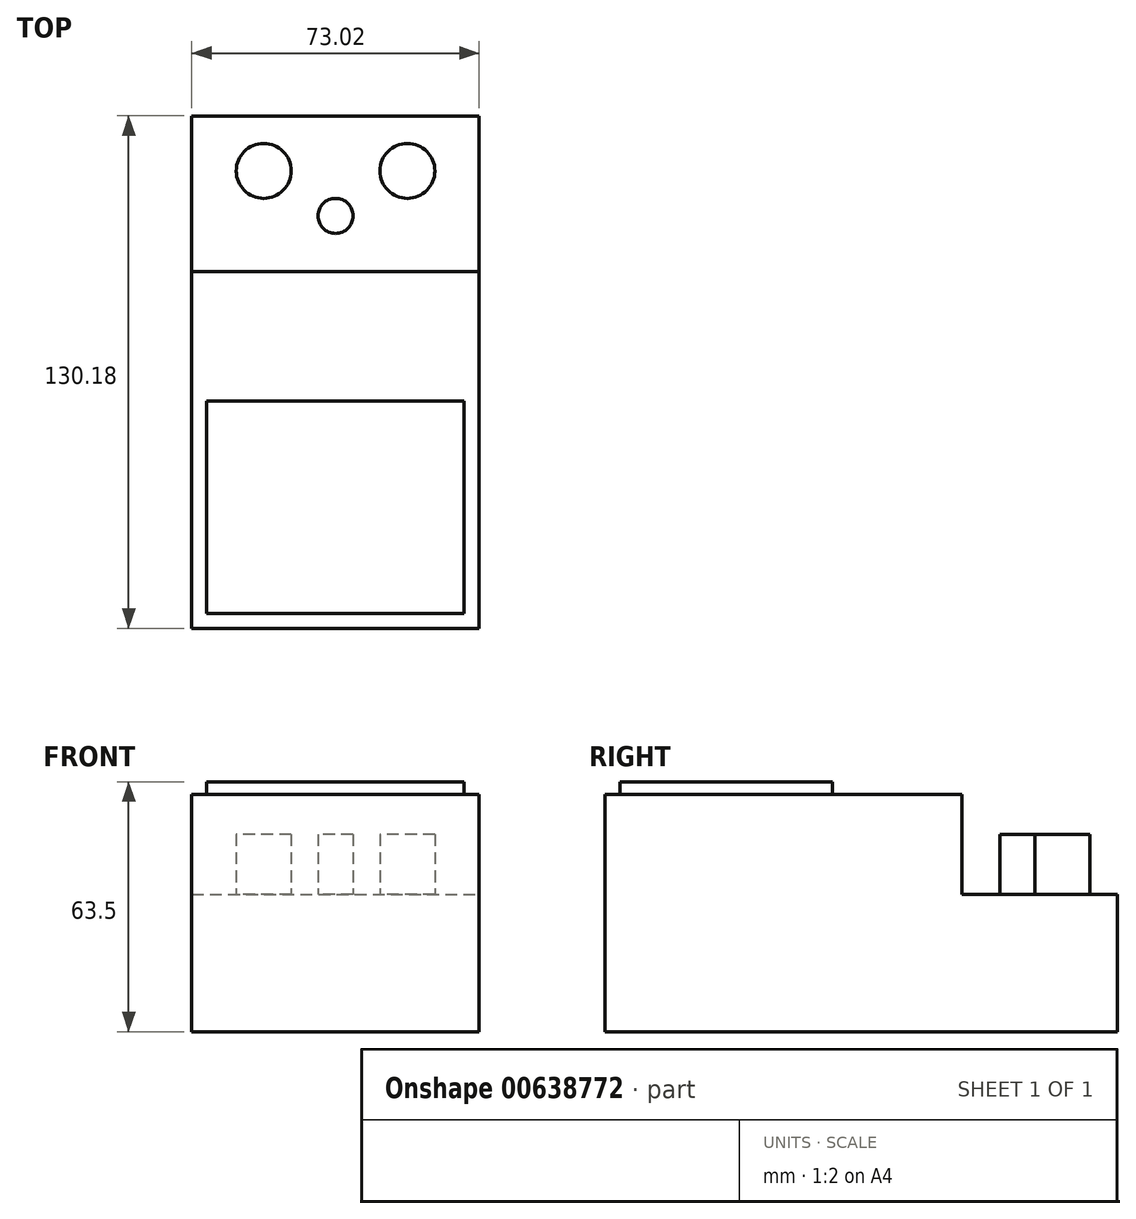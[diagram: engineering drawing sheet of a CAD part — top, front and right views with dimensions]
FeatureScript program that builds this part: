
annotation { "Feature Type Name" : "Feature", "Feature Type Description" : "" }
export const myFeature = defineFeature(function(context is Context, id is Id, definition is map)
    precondition{}
    {
        {
            var Q0;
            Q0=qCreatedBy(makeId("Top.planeOp"),FACE);
            var sketch = newSketch(context, id + "F0", { "sketchPlane" : qUnion([Q0])});
            skLineSegment(sketch, "E0.bottom", {"start": v(-36.51, 65.09) * mm, "end": v(36.51, 65.09) * mm});
            skLineSegment(sketch, "E0.top", {"start": v(-36.51, -65.09) * mm, "end": v(36.51, -65.09) * mm});
            skLineSegment(sketch, "E0.left", {"start": v(-36.51, 65.09) * mm, "end": v(-36.51, -65.09) * mm});
            skLineSegment(sketch, "E0.right", {"start": v(36.51, 65.09) * mm, "end": v(36.51, -65.09) * mm});
            skPoint(sketch, "E0.middle", {"position": v(0, 0) * mm});
            skLineSegment(sketch, "E1", {"start": v(-36.51, 25.5) * mm, "end": v(36.51, 25.5) * mm});
            skSolve(sketch);
        }
        {
            var Q0;
            {var subQ0=sQuery(id+"F0.wireOp",EDGE,"E0.top");Q0=makeQuery(id+"F0.imprint","IMPRINT",FACE,{"disambiguationData":[TD([[makeQuery(id+"F0.imprint","IMPRINT",EDGE,{"derivedFrom":subQ0}),1.0]])]});}
            extrude(context, id + "F1", {"entities" : qUnion([Q0]), "depth" : 60.32 * mm, "offsetDistance" : 25.4 * mm});
        }
        {
            var Q0;
            Q0 = qSketchRegion(id + "F0", true);
            extrude(context, id + "F2", {"entities" : qUnion([Q0]), "operationType" : NewBodyOperationType.ADD, "depth" : 34.92 * mm, "offsetDistance" : 25.4 * mm});
        }
        {
            var Q0;
            Q0=makeQuery(id+"F1.opExtrude","CAP_FACE",FACE,{"disambiguationData":[OSD([sQuery(id+"F0.wireOp",EDGE,"E0.top"),sQuery(id+"F0.wireOp",EDGE,"E0.left"),sQuery(id+"F0.wireOp",EDGE,"E0.right"),sQuery(id+"F0.wireOp",EDGE,"E1")])],"isStart":false});
            var sketch = newSketch(context, id + "F3", { "sketchPlane" : qUnion([Q0])});
            skLineSegment(sketch, "E2.bottom", {"start": v(-32.7, -61.28) * mm, "end": v(32.7, -61.28) * mm});
            skLineSegment(sketch, "E2.top", {"start": v(-32.7, -7.32) * mm, "end": v(32.7, -7.32) * mm});
            skLineSegment(sketch, "E2.left", {"start": v(-32.7, -61.28) * mm, "end": v(-32.7, -7.32) * mm});
            skLineSegment(sketch, "E2.right", {"start": v(32.7, -61.28) * mm, "end": v(32.7, -7.32) * mm});
            skSolve(sketch);
        }
        {
            var Q0;
            Q0=makeQuery(id+"F3.imprint","IMPRINT",FACE,{"disambiguationData":[TD([[makeQuery(id+"F3.imprint","IMPRINT",EDGE,{"derivedFrom":sQuery(id+"F3.wireOp",EDGE,"E2.bottom")}),1.0]])]});
            extrude(context, id + "F4", {"entities" : qUnion([Q0]), "operationType" : NewBodyOperationType.ADD, "depth" : 3.17 * mm, "offsetDistance" : 25.4 * mm});
        }
        {
            var Q0;
            Q0=makeQuery(id+"F2.opExtrude","CAP_FACE",FACE,{"disambiguationData":[OSD([sQuery(id+"F0.wireOp",EDGE,"E0.bottom"),sQuery(id+"F0.wireOp",EDGE,"E0.top"),sQuery(id+"F0.wireOp",EDGE,"E0.left"),sQuery(id+"F0.wireOp",EDGE,"E0.right")])],"isStart":false});
            var sketch = newSketch(context, id + "F5", { "sketchPlane" : qUnion([Q0])});
            skCircle(sketch, "E3", {"center": v(-18.26, 51.12) * mm, "radius": 6.99 * mm});
            skCircle(sketch, "E4", {"center": v(18.26, 51.12) * mm, "radius": 6.99 * mm});
            skCircle(sketch, "E5", {"center": v(0, 39.69) * mm, "radius": 4.45 * mm});
            skSolve(sketch);
        }
        {
            var Q0;
            Q0=makeQuery(id+"F5.imprint","IMPRINT",FACE,{"disambiguationData":[TD([[makeQuery(id+"F5.imprint","IMPRINT",EDGE,{"derivedFrom":sQuery(id+"F5.wireOp",EDGE,"E3")}),1.0]])]});
            var Q1;
            Q1=makeQuery(id+"F5.imprint","IMPRINT",FACE,{"disambiguationData":[TD([[makeQuery(id+"F5.imprint","IMPRINT",EDGE,{"derivedFrom":sQuery(id+"F5.wireOp",EDGE,"E5")}),1.0]])]});
            var Q2;
            Q2=makeQuery(id+"F5.imprint","IMPRINT",FACE,{"disambiguationData":[TD([[makeQuery(id+"F5.imprint","IMPRINT",EDGE,{"derivedFrom":sQuery(id+"F5.wireOp",EDGE,"E4")}),1.0]])]});
            extrude(context, id + "F6", {"entities" : qUnion([Q0, Q1, Q2]), "operationType" : NewBodyOperationType.ADD, "depth" : 15.24 * mm, "offsetDistance" : 25.4 * mm});
        }
    });
